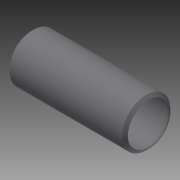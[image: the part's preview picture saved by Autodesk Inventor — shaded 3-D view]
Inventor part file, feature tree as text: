
AUTODESK INVENTOR PART (.ipt)
format: ipt  version: 2014 (Build 180170000, 170)  size: 129,024 bytes
history: native  units: in
note: dims shown in document units (in); Inventor stores cm internally (conversion verified against a paired STEP export)
features: other x56, revolve x1, sketch x1
ambient origin geometry x8: Origin, YZ Plane, XZ Plane, XY Plane, X Axis, Y Axis, Z Axis, Center Point
bodies: Solid1 (feature_tree)
feature tree (58):
  revolve  "Revolution1"  [1 undecoded]
  other  "o1_XY"
  other  "o1_YZ"
  other  "o1_ZX"
  other  "o1_X"
  other  "o1_Y"
  other  "o1_Z"
  other  "o1_Center"
  other  "o2_XY"
  other  "o2_YZ"
  other  "o2_ZX"
  other  "o2_X"
  other  "o2_Y"
  other  "o2_Z"
  other  "o2_Center"
  other  "t1_XY"
  other  "t1_YZ"
  other  "t1_ZX"
  other  "t1_X"
  other  "t1_Y"
  other  "t1_Z"
  other  "t1_Center"
  other  "t2_XY"
  other  "t2_YZ"
  other  "t2_ZX"
  other  "t2_X"
  other  "t2_Y"
  other  "t2_Z"
  other  "t2_Center"
  other  "t3_XY"
  other  "t3_YZ"
  other  "t3_ZX"
  other  "t3_X"
  other  "t3_Y"
  other  "t3_Z"
  other  "t3_Center"
  other  "t4_XY"
  other  "t4_YZ"
  other  "t4_ZX"
  other  "t4_X"
  other  "t4_Y"
  other  "t4_Z"
  other  "t4_Center"
  other  "tube1_XY"
  other  "tube1_YZ"
  other  "tube1_ZX"
  other  "tube1_X"
  other  "tube1_Y"
  other  "tube1_Z"
  other  "tube1_Center"
  other  "tube2_XY"
  other  "tube2_YZ"
  other  "tube2_ZX"
  other  "tube2_X"
  other  "tube2_Y"
  other  "tube2_Z"
  other  "tube2_Center"
  sketch  "Sketch_5"  dims[d0=360.0deg]
note: 1 required parameter value undecoded (feature->parameter linkage not recoverable at this tier; creation-order binding heuristic only, values carry confidence <= 0.55)
